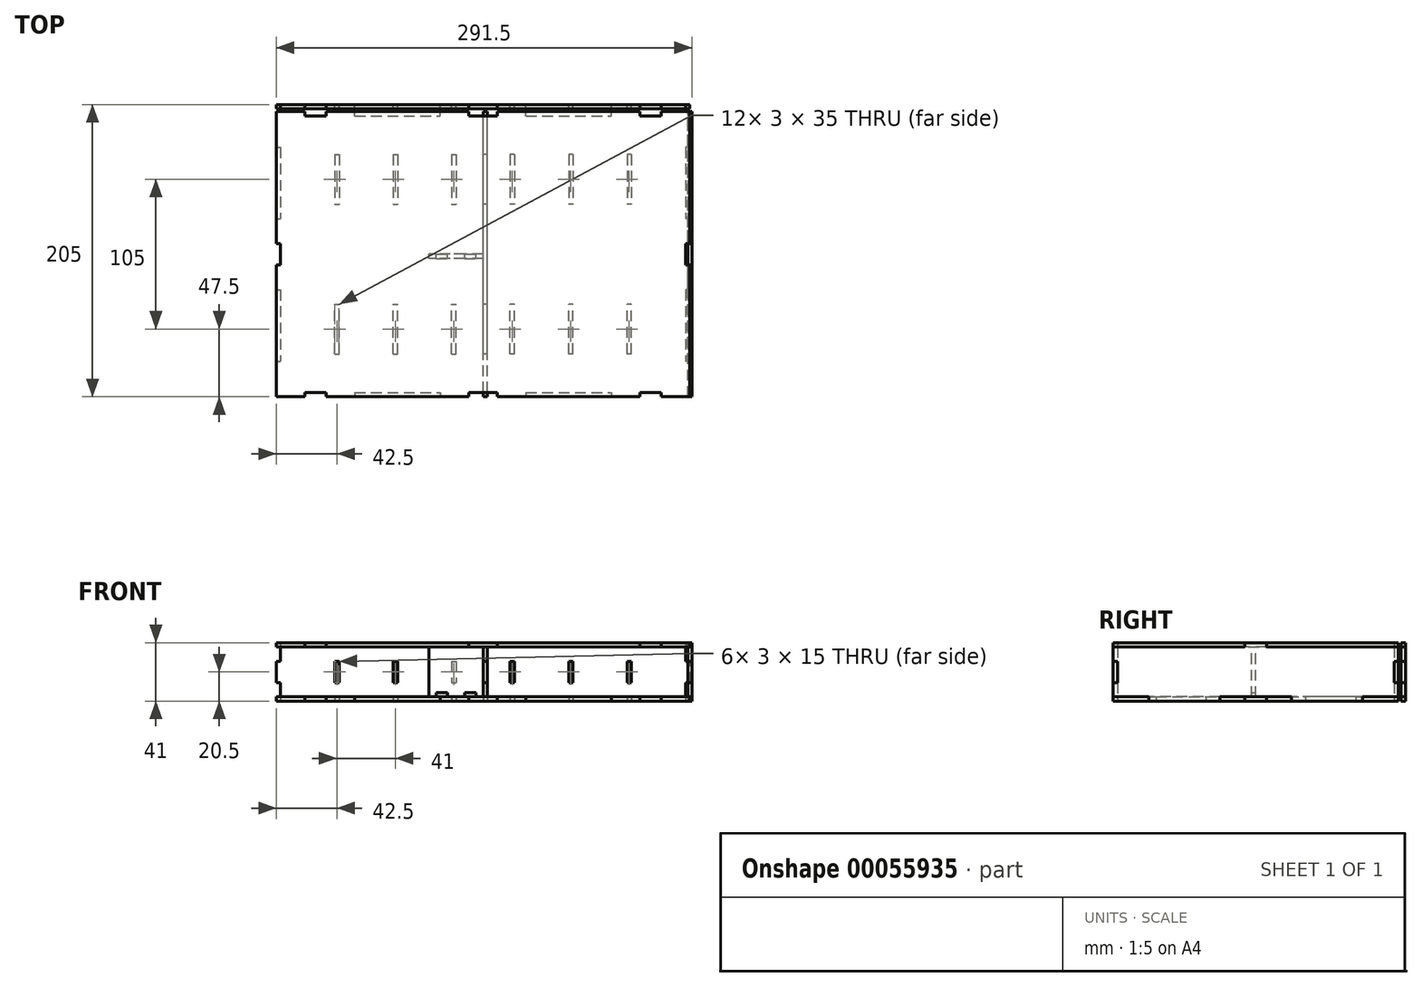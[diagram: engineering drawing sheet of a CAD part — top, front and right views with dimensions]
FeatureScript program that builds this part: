
annotation { "Feature Type Name" : "Feature", "Feature Type Description" : "" }
export const myFeature = defineFeature(function(context is Context, id is Id, definition is map)
    precondition{}
    {
        {
            assignVariable(context, id + "F0", {"name" : "WoodWidth", "anyValue" : 3});
        }
        {
            var Q0;
            Q0=qCreatedBy(makeId("Top.planeOp"),FACE);
            var sketch = newSketch(context, id + "F1", { "sketchPlane" : qUnion([Q0])});
            skLineSegment(sketch, "E0.bottom", {"start": v(-145, 100) * mm, "end": v(-125, 100) * mm});
            skLineSegment(sketch, "E0.top", {"start": v(-145, -100) * mm, "end": v(-125, -100) * mm});
            skLineSegment(sketch, "E0.left", {"start": v(-145, 100) * mm, "end": v(-145, 75) * mm});
            skLineSegment(sketch, "E0.right", {"start": v(145, 100) * mm, "end": v(145, 75) * mm});
            skLineSegment(sketch, "E1.bottom", {"start": v(-125, 97) * mm, "end": v(-110, 97) * mm});
            skLineSegment(sketch, "E1.top", {"start": v(-125, -97) * mm, "end": v(-110, -97) * mm});
            skLineSegment(sketch, "E1.left", {"start": v(-142, 75) * mm, "end": v(-142, 25) * mm});
            skLineSegment(sketch, "E1.right", {"start": v(142, 75) * mm, "end": v(142, 25) * mm});
            skLineSegment(sketch, "E2.bottom", {"start": v(-145, 75) * mm, "end": v(-142, 75) * mm});
            skLineSegment(sketch, "E2.top", {"start": v(-145, 25) * mm, "end": v(-142, 25) * mm});
            skLineSegment(sketch, "E3.MirrorCS", {"start": v(-145, -25) * mm, "end": v(-142, -25) * mm});
            skLineSegment(sketch, "E4.MirrorCS", {"start": v(-145, -75) * mm, "end": v(-142, -75) * mm});
            skLineSegment(sketch, "E5.MirrorCS", {"start": v(145, 75) * mm, "end": v(142, 75) * mm});
            skLineSegment(sketch, "E6.MirrorCS", {"start": v(145, 25) * mm, "end": v(142, 25) * mm});
            skLineSegment(sketch, "E7.MirrorCS", {"start": v(145, -25) * mm, "end": v(142, -25) * mm});
            skLineSegment(sketch, "E8.MirrorCS", {"start": v(145, -75) * mm, "end": v(142, -75) * mm});
            skLineSegment(sketch, "E9", {"start": v(-30, 97) * mm, "end": v(-30, 100) * mm});
            skLineSegment(sketch, "E10", {"start": v(-90, 97) * mm, "end": v(-90, 100) * mm});
            skLineSegment(sketch, "E11.MirrorCS", {"start": v(30, 97) * mm, "end": v(30, 100) * mm});
            skLineSegment(sketch, "E12.MirrorCS", {"start": v(90, 97) * mm, "end": v(90, 100) * mm});
            skLineSegment(sketch, "E13.MirrorCS", {"start": v(-30, -97) * mm, "end": v(-30, -100) * mm});
            skLineSegment(sketch, "E14.MirrorCS", {"start": v(-90, -97) * mm, "end": v(-90, -100) * mm});
            skLineSegment(sketch, "E15.MirrorCS", {"start": v(30, -97) * mm, "end": v(30, -100) * mm});
            skLineSegment(sketch, "E16.MirrorCS", {"start": v(90, -97) * mm, "end": v(90, -100) * mm});
            skLineSegment(sketch, "E17.trimOffspring", {"start": v(-30, 100) * mm, "end": v(-10, 100) * mm});
            skLineSegment(sketch, "E18.trimOffspring", {"start": v(90, 100) * mm, "end": v(110, 100) * mm});
            skLineSegment(sketch, "E19.trimOffspring", {"start": v(-145, 25) * mm, "end": v(-145, 7.5) * mm});
            skLineSegment(sketch, "E20.trimOffspring", {"start": v(-145, -75) * mm, "end": v(-145, -100) * mm});
            skLineSegment(sketch, "E21.trimOffspring", {"start": v(-30, -100) * mm, "end": v(-10, -100) * mm});
            skLineSegment(sketch, "E22.trimOffspring", {"start": v(90, -100) * mm, "end": v(110, -100) * mm});
            skLineSegment(sketch, "E23.trimOffspring", {"start": v(145, -75) * mm, "end": v(145, -100) * mm});
            skLineSegment(sketch, "E24.trimOffspring", {"start": v(145, 25) * mm, "end": v(145, 7.5) * mm});
            skLineSegment(sketch, "E25", {"start": v(-10, 100) * mm, "end": v(-10, 97) * mm});
            skLineSegment(sketch, "E26", {"start": v(-145, 7.5) * mm, "end": v(-142, 7.5) * mm});
            skLineSegment(sketch, "E27", {"start": v(-125, 100) * mm, "end": v(-125, 97) * mm});
            skLineSegment(sketch, "E28", {"start": v(-110, 100) * mm, "end": v(-110, 97) * mm});
            skLineSegment(sketch, "E29.MirrorCS", {"start": v(145, 7.5) * mm, "end": v(142, 7.5) * mm});
            skLineSegment(sketch, "E30.MirrorCS", {"start": v(10, 100) * mm, "end": v(10, 97) * mm});
            skLineSegment(sketch, "E31.MirrorCS", {"start": v(110, 100) * mm, "end": v(110, 97) * mm});
            skLineSegment(sketch, "E32.MirrorCS", {"start": v(125, 100) * mm, "end": v(125, 97) * mm});
            skLineSegment(sketch, "E33.MirrorCS", {"start": v(-145, -7.5) * mm, "end": v(-142, -7.5) * mm});
            skLineSegment(sketch, "E34.MirrorCS", {"start": v(-125, -100) * mm, "end": v(-125, -97) * mm});
            skLineSegment(sketch, "E35.MirrorCS", {"start": v(-110, -100) * mm, "end": v(-110, -97) * mm});
            skLineSegment(sketch, "E36.MirrorCS", {"start": v(-10, -100) * mm, "end": v(-10, -97) * mm});
            skLineSegment(sketch, "E37.MirrorCS", {"start": v(10, -100) * mm, "end": v(10, -97) * mm});
            skLineSegment(sketch, "E38.MirrorCS", {"start": v(110, -100) * mm, "end": v(110, -97) * mm});
            skLineSegment(sketch, "E39.MirrorCS", {"start": v(125, -100) * mm, "end": v(125, -97) * mm});
            skLineSegment(sketch, "E40.MirrorCS", {"start": v(145, -7.5) * mm, "end": v(142, -7.5) * mm});
            skLineSegment(sketch, "E41.trimOffspring", {"start": v(-110, 100) * mm, "end": v(-90, 100) * mm});
            skLineSegment(sketch, "E42.trimOffspring", {"start": v(10, 100) * mm, "end": v(30, 100) * mm});
            skLineSegment(sketch, "E43.trimOffspring", {"start": v(125, 100) * mm, "end": v(145, 100) * mm});
            skLineSegment(sketch, "E44.trimOffspring", {"start": v(145, -7.5) * mm, "end": v(145, -25) * mm});
            skLineSegment(sketch, "E45.trimOffspring", {"start": v(125, -100) * mm, "end": v(145, -100) * mm});
            skLineSegment(sketch, "E46.trimOffspring", {"start": v(10, -100) * mm, "end": v(30, -100) * mm});
            skLineSegment(sketch, "E47.trimOffspring", {"start": v(-110, -100) * mm, "end": v(-90, -100) * mm});
            skLineSegment(sketch, "E48.trimOffspring", {"start": v(-145, -7.5) * mm, "end": v(-145, -25) * mm});
            skPoint(sketch, "E49.orphan", {"position": v(-142, 97) * mm});
            skLineSegment(sketch, "E50.trimOffspring", {"start": v(-90, 97) * mm, "end": v(-30, 97) * mm});
            skLineSegment(sketch, "E51.trimOffspring", {"start": v(-10, 97) * mm, "end": v(10, 97) * mm});
            skLineSegment(sketch, "E52.trimOffspring", {"start": v(30, 97) * mm, "end": v(90, 97) * mm});
            skLineSegment(sketch, "E53.trimOffspring", {"start": v(110, 97) * mm, "end": v(125, 97) * mm});
            skLineSegment(sketch, "E54.trimOffspring", {"start": v(142, 7.5) * mm, "end": v(142, -7.5) * mm});
            skLineSegment(sketch, "E55.trimOffspring", {"start": v(142, -25) * mm, "end": v(142, -75) * mm});
            skLineSegment(sketch, "E56.trimOffspring", {"start": v(110, -97) * mm, "end": v(125, -97) * mm});
            skLineSegment(sketch, "E57.trimOffspring", {"start": v(30, -97) * mm, "end": v(90, -97) * mm});
            skLineSegment(sketch, "E58.trimOffspring", {"start": v(-10, -97) * mm, "end": v(10, -97) * mm});
            skLineSegment(sketch, "E59.trimOffspring", {"start": v(-90, -97) * mm, "end": v(-30, -97) * mm});
            skLineSegment(sketch, "E60.trimOffspring", {"start": v(-142, -25) * mm, "end": v(-142, -75) * mm});
            skLineSegment(sketch, "E61.trimOffspring", {"start": v(-142, 7.5) * mm, "end": v(-142, -7.5) * mm});
            skLineSegment(sketch, "E62.bottom", {"start": v(-104, 70) * mm, "end": v(-101, 70) * mm});
            skLineSegment(sketch, "E62.top", {"start": v(-104, 35) * mm, "end": v(-101, 35) * mm});
            skLineSegment(sketch, "E62.left", {"start": v(-104, 70) * mm, "end": v(-104, 35) * mm});
            skLineSegment(sketch, "E62.right", {"start": v(-101, 70) * mm, "end": v(-101, 35) * mm});
            skLineSegment(sketch, "E63.MirrorCS", {"start": v(-104, -35) * mm, "end": v(-101, -35) * mm});
            skLineSegment(sketch, "E64.MirrorCS", {"start": v(-101, -70) * mm, "end": v(-101, -35) * mm});
            skLineSegment(sketch, "E65.MirrorCS", {"start": v(-104, -70) * mm, "end": v(-104, -35) * mm});
            skLineSegment(sketch, "E66.MirrorCS", {"start": v(-104, -70) * mm, "end": v(-101, -70) * mm});
            skLineSegment(sketch, "E67.MirrorCS", {"start": v(104, 35) * mm, "end": v(101, 35) * mm});
            skLineSegment(sketch, "E68.MirrorCS", {"start": v(104, 70) * mm, "end": v(101, 70) * mm});
            skLineSegment(sketch, "E69.MirrorCS", {"start": v(101, 70) * mm, "end": v(101, 35) * mm});
            skLineSegment(sketch, "E70.MirrorCS", {"start": v(104, 70) * mm, "end": v(104, 35) * mm});
            skLineSegment(sketch, "E71.MirrorCS", {"start": v(104, -35) * mm, "end": v(101, -35) * mm});
            skLineSegment(sketch, "E72.MirrorCS", {"start": v(104, -70) * mm, "end": v(101, -70) * mm});
            skLineSegment(sketch, "E73.MirrorCS", {"start": v(101, -70) * mm, "end": v(101, -35) * mm});
            skLineSegment(sketch, "E74.MirrorCS", {"start": v(104, -70) * mm, "end": v(104, -35) * mm});
            skLineSegment(sketch, "E75.right", {"start": v(-63, 70) * mm, "end": v(-63, 35) * mm});
            skLineSegment(sketch, "E75.left", {"start": v(-60, 70) * mm, "end": v(-60, 35) * mm});
            skLineSegment(sketch, "E75.top", {"start": v(-63, 35) * mm, "end": v(-60, 35) * mm});
            skLineSegment(sketch, "E75.bottom", {"start": v(-63, 70) * mm, "end": v(-60, 70) * mm});
            skLineSegment(sketch, "E76.MirrorCS", {"start": v(63, 70) * mm, "end": v(60, 70) * mm});
            skLineSegment(sketch, "E77.MirrorCS", {"start": v(63, 35) * mm, "end": v(60, 35) * mm});
            skLineSegment(sketch, "E78.MirrorCS", {"start": v(60, 70) * mm, "end": v(60, 35) * mm});
            skLineSegment(sketch, "E79.MirrorCS", {"start": v(63, 70) * mm, "end": v(63, 35) * mm});
            skLineSegment(sketch, "E80.MirrorCS", {"start": v(63, -35) * mm, "end": v(60, -35) * mm});
            skLineSegment(sketch, "E81.MirrorCS", {"start": v(-63, -70) * mm, "end": v(-60, -70) * mm});
            skLineSegment(sketch, "E82.MirrorCS", {"start": v(63, -70) * mm, "end": v(60, -70) * mm});
            skLineSegment(sketch, "E83.MirrorCS", {"start": v(-63, -35) * mm, "end": v(-60, -35) * mm});
            skLineSegment(sketch, "E84.MirrorCS", {"start": v(60, -70) * mm, "end": v(60, -35) * mm});
            skLineSegment(sketch, "E85.MirrorCS", {"start": v(-63, -70) * mm, "end": v(-63, -35) * mm});
            skLineSegment(sketch, "E86.MirrorCS", {"start": v(63, -70) * mm, "end": v(63, -35) * mm});
            skLineSegment(sketch, "E87.MirrorCS", {"start": v(-60, -70) * mm, "end": v(-60, -35) * mm});
            skLineSegment(sketch, "E88.right", {"start": v(-22, 70) * mm, "end": v(-22, 35) * mm});
            skLineSegment(sketch, "E88.left", {"start": v(-19, 70) * mm, "end": v(-19, 35) * mm});
            skLineSegment(sketch, "E88.bottom", {"start": v(-22, 70) * mm, "end": v(-19, 70) * mm});
            skLineSegment(sketch, "E88.top", {"start": v(-22, 35) * mm, "end": v(-19, 35) * mm});
            skLineSegment(sketch, "E89.MirrorCS", {"start": v(22, 35) * mm, "end": v(19, 35) * mm});
            skLineSegment(sketch, "E90.MirrorCS", {"start": v(22, 70) * mm, "end": v(19, 70) * mm});
            skLineSegment(sketch, "E91.MirrorCS", {"start": v(19, 70) * mm, "end": v(19, 35) * mm});
            skLineSegment(sketch, "E92.MirrorCS", {"start": v(22, 70) * mm, "end": v(22, 35) * mm});
            skLineSegment(sketch, "E93.MirrorCS", {"start": v(-22, -35) * mm, "end": v(-19, -35) * mm});
            skLineSegment(sketch, "E94.MirrorCS", {"start": v(22, -35) * mm, "end": v(19, -35) * mm});
            skLineSegment(sketch, "E95.MirrorCS", {"start": v(22, -70) * mm, "end": v(19, -70) * mm});
            skLineSegment(sketch, "E96.MirrorCS", {"start": v(-22, -70) * mm, "end": v(-19, -70) * mm});
            skLineSegment(sketch, "E97.MirrorCS", {"start": v(22, -70) * mm, "end": v(22, -35) * mm});
            skLineSegment(sketch, "E98.MirrorCS", {"start": v(-22, -70) * mm, "end": v(-22, -35) * mm});
            skLineSegment(sketch, "E99.MirrorCS", {"start": v(-19, -70) * mm, "end": v(-19, -35) * mm});
            skLineSegment(sketch, "E100.MirrorCS", {"start": v(19, -70) * mm, "end": v(19, -35) * mm});
            skSolve(sketch);
        }
        {
            var Q0;
            {var subQ13=sQuery(id+"F1.wireOp",EDGE,"E1.left");Q0=makeQuery(id+"F1.imprint","IMPRINT",FACE,{"disambiguationData":[TD([[makeQuery(id+"F1.imprint","IMPRINT",EDGE,{"derivedFrom":subQ13}),1.0]])]});}
            var Q1;
            Q1=makeQuery(id+"F1.imprint","IMPRINT",FACE,{"disambiguationData":[TD([[makeQuery(id+"F1.imprint","IMPRINT",EDGE,{"derivedFrom":sQuery(id+"F1.wireOp",EDGE,"E0.bottom")}),-1.0]])]});
            var Q2;
            {var subQ0=sQuery(id+"F1.wireOp",EDGE,"E9");Q2=makeQuery(id+"F1.imprint","IMPRINT",FACE,{"disambiguationData":[TD([[makeQuery(id+"F1.imprint","IMPRINT",EDGE,{"derivedFrom":subQ0}),-1.0]])]});}
            var Q3;
            Q3=makeQuery(id+"F1.imprint","IMPRINT",FACE,{"disambiguationData":[TD([[makeQuery(id+"F1.imprint","IMPRINT",EDGE,{"derivedFrom":sQuery(id+"F1.wireOp",EDGE,"E0.right")}),-1.0]])]});
            var Q4;
            {var subQ0=sQuery(id+"F1.wireOp",EDGE,"E6.MirrorCS");Q4=makeQuery(id+"F1.imprint","IMPRINT",FACE,{"disambiguationData":[TD([[makeQuery(id+"F1.imprint","IMPRINT",EDGE,{"derivedFrom":subQ0}),1.0]])]});}
            var Q5;
            {var subQ1=sQuery(id+"F1.wireOp",EDGE,"E8.MirrorCS");Q5=makeQuery(id+"F1.imprint","IMPRINT",FACE,{"disambiguationData":[TD([[makeQuery(id+"F1.imprint","IMPRINT",EDGE,{"derivedFrom":subQ1}),1.0]])]});}
            var Q6;
            {var subQ0=sQuery(id+"F1.wireOp",EDGE,"E13.MirrorCS");Q6=makeQuery(id+"F1.imprint","IMPRINT",FACE,{"disambiguationData":[TD([[makeQuery(id+"F1.imprint","IMPRINT",EDGE,{"derivedFrom":subQ0}),1.0]])]});}
            var Q7;
            Q7=makeQuery(id+"F1.imprint","IMPRINT",FACE,{"disambiguationData":[TD([[makeQuery(id+"F1.imprint","IMPRINT",EDGE,{"derivedFrom":sQuery(id+"F1.wireOp",EDGE,"E0.top")}),1.0]])]});
            var Q8;
            {var subQ0=sQuery(id+"F1.wireOp",EDGE,"E2.top");Q8=makeQuery(id+"F1.imprint","IMPRINT",FACE,{"disambiguationData":[TD([[makeQuery(id+"F1.imprint","IMPRINT",EDGE,{"derivedFrom":subQ0}),-1.0]])]});}
            extrude(context, id + "F2", {"entities" : qUnion([Q0, Q1, Q2, Q3, Q4, Q5, Q6, Q7, Q8]), "depth" : (getVariable(context, 'WoodWidth')) * mm});
        }
        {
            var Q0;
            Q0=qCreatedBy(makeId("Right.planeOp"),FACE);
            var sketch = newSketch(context, id + "F3", { "sketchPlane" : qUnion([Q0])});
            skLineSegment(sketch, "E101.top", {"start": v(-100, 38) * mm, "end": v(-7.5, 38) * mm});
            skLineSegment(sketch, "E101.left", {"start": v(-100, 3) * mm, "end": v(-100, 13) * mm});
            skLineSegment(sketch, "E101.right", {"start": v(100, 3) * mm, "end": v(100, 13) * mm});
            skLineSegment(sketch, "E102", {"start": v(-75, 3) * mm, "end": v(-75, 0) * mm});
            skLineSegment(sketch, "E103", {"start": v(-25, 3) * mm, "end": v(-25, 0) * mm});
            skLineSegment(sketch, "E104.MirrorCS", {"start": v(25, 3) * mm, "end": v(25, 0) * mm});
            skLineSegment(sketch, "E105.MirrorCS", {"start": v(75, 3) * mm, "end": v(75, 0) * mm});
            skLineSegment(sketch, "E106", {"start": v(-97, 28) * mm, "end": v(-97, 13) * mm});
            skLineSegment(sketch, "E107", {"start": v(-100, 28) * mm, "end": v(-97, 28) * mm});
            skLineSegment(sketch, "E108", {"start": v(-100, 13) * mm, "end": v(-97, 13) * mm});
            skLineSegment(sketch, "E109.MirrorCS", {"start": v(100, 13) * mm, "end": v(97, 13) * mm});
            skLineSegment(sketch, "E110.MirrorCS", {"start": v(100, 28) * mm, "end": v(97, 28) * mm});
            skLineSegment(sketch, "E111.MirrorCS", {"start": v(97, 28) * mm, "end": v(97, 13) * mm});
            skLineSegment(sketch, "E112.trimOffspring", {"start": v(-100, 28) * mm, "end": v(-100, 38) * mm});
            skPoint(sketch, "E113.orphan", {"position": v(-100, 3) * mm});
            skPoint(sketch, "E114.orphan", {"position": v(-97, 0) * mm});
            skLineSegment(sketch, "E115.trimOffspring", {"start": v(100, 28) * mm, "end": v(100, 38) * mm});
            skPoint(sketch, "E116.orphan", {"position": v(97, 38) * mm});
            skPoint(sketch, "E117.trimOffspring.end.orphan", {"position": v(97, 0) * mm});
            skPoint(sketch, "E118.orphan", {"position": v(-97, 38) * mm});
            skLineSegment(sketch, "E119", {"start": v(-100, 3) * mm, "end": v(-75, 3) * mm});
            skLineSegment(sketch, "E120", {"start": v(75, 0) * mm, "end": v(25, 0) * mm});
            skPoint(sketch, "E121.orphan", {"position": v(-100, 0) * mm});
            skLineSegment(sketch, "E122.trimOffspring", {"start": v(-25, 0) * mm, "end": v(-75, 0) * mm});
            skLineSegment(sketch, "E123.trimOffspring", {"start": v(75, 3) * mm, "end": v(100, 3) * mm});
            skLineSegment(sketch, "E124", {"start": v(-7.5, 38) * mm, "end": v(-7.5, 41) * mm});
            skLineSegment(sketch, "E125", {"start": v(-7.5, 41) * mm, "end": v(0, 41) * mm});
            skLineSegment(sketch, "E126.MirrorCS", {"start": v(7.5, 41) * mm, "end": v(0, 41) * mm});
            skLineSegment(sketch, "E127.MirrorCS", {"start": v(7.5, 38) * mm, "end": v(7.5, 41) * mm});
            skLineSegment(sketch, "E128.trimOffspring", {"start": v(7.5, 38) * mm, "end": v(100, 38) * mm});
            skLineSegment(sketch, "E129", {"start": v(-25, 3) * mm, "end": v(25, 3) * mm});
            skSolve(sketch);
        }
        {
            var Q0;
            Q0=makeQuery(id+"F3.imprint","IMPRINT",FACE,{"disambiguationData":[TD([[makeQuery(id+"F3.imprint","IMPRINT",EDGE,{"derivedFrom":sQuery(id+"F3.wireOp",EDGE,"E101.top")}),-1.0]])]});
            extrude(context, id + "F4", {"entities" : qUnion([Q0]), "depth" : (getVariable(context, 'WoodWidth')) * mm});
        }
        {
            var Q0;
            Q0=makeQuery(id+"F4.opExtrude","SWEPT_BODY",BODY,{"disambiguationData":[OSD([sQuery(id+"F3.wireOp",EDGE,"E101.top"),sQuery(id+"F3.wireOp",EDGE,"E101.left"),sQuery(id+"F3.wireOp",EDGE,"E101.right"),sQuery(id+"F3.wireOp",EDGE,"E102"),sQuery(id+"F3.wireOp",EDGE,"E103"),sQuery(id+"F3.wireOp",EDGE,"cdd6de69-b75f-463d-88d1-304e89352a25"),sQuery(id+"F3.wireOp",EDGE,"cb626959-0f36-4611-9174-e5582c259fc60.MirrorCS"),sQuery(id+"F3.wireOp",EDGE,"E104.MirrorCS"),sQuery(id+"F3.wireOp",EDGE,"E105.MirrorCS"),sQuery(id+"F3.wireOp",EDGE,"E106"),sQuery(id+"F3.wireOp",EDGE,"E107"),sQuery(id+"F3.wireOp",EDGE,"E108"),sQuery(id+"F3.wireOp",EDGE,"E109.MirrorCS"),sQuery(id+"F3.wireOp",EDGE,"E110.MirrorCS"),sQuery(id+"F3.wireOp",EDGE,"E111.MirrorCS"),sQuery(id+"F3.wireOp",EDGE,"E112.trimOffspring"),sQuery(id+"F3.wireOp",EDGE,"E115.trimOffspring"),sQuery(id+"F3.wireOp",EDGE,"E119"),sQuery(id+"F3.wireOp",EDGE,"E120"),sQuery(id+"F3.wireOp",EDGE,"E122.trimOffspring"),sQuery(id+"F3.wireOp",EDGE,"c6658c1a-ea69-4595-8e1a-c0dab725dcbe.trimOffspring"),sQuery(id+"F3.wireOp",EDGE,"E123.trimOffspring"),sQuery(id+"F3.wireOp",EDGE,"9fd187d6-3b35-4cf2-808b-338c497833ee.trimOffspring"),sQuery(id+"F3.wireOp",EDGE,"23121bdd-483d-45c2-8d1b-d883080a6cf4.trimOffspring"),sQuery(id+"F3.wireOp",EDGE,"E124"),sQuery(id+"F3.wireOp",EDGE,"E125"),sQuery(id+"F3.wireOp",EDGE,"E126.MirrorCS"),sQuery(id+"F3.wireOp",EDGE,"E127.MirrorCS"),sQuery(id+"F3.wireOp",EDGE,"E128.trimOffspring")])]});
            transform(context, id + "F5", {"entities" : qUnion([Q0]), "transformType" : TransformType.TRANSLATION_3D, "dx" : (297 / 2 - 5) * mm, "dy" : 0 * mm, "dz" : 0 * mm, "makeCopy" : false});
        }
        {
            var Q0;
            Q0=qCreatedBy(makeId("Front.planeOp"),FACE);
            var sketch = newSketch(context, id + "F6", { "sketchPlane" : qUnion([Q0])});
            skLineSegment(sketch, "E130.top", {"start": v(-142, 38) * mm, "end": v(-125, 38) * mm});
            skLineSegment(sketch, "E130.left", {"start": v(-145, 13) * mm, "end": v(-145, 28) * mm});
            skLineSegment(sketch, "E131", {"start": v(142, 38) * mm, "end": v(142, 28) * mm});
            skLineSegment(sketch, "E132", {"start": v(-30, 3) * mm, "end": v(-30, 0) * mm});
            skLineSegment(sketch, "E133", {"start": v(-90, 3) * mm, "end": v(-90, 0) * mm});
            skLineSegment(sketch, "E134", {"start": v(142, 28) * mm, "end": v(145, 28) * mm});
            skLineSegment(sketch, "E135", {"start": v(145, 13) * mm, "end": v(142, 13) * mm});
            skLineSegment(sketch, "E136.MirrorCS", {"start": v(30, 3) * mm, "end": v(30, 0) * mm});
            skLineSegment(sketch, "E137.MirrorCS", {"start": v(90, 3) * mm, "end": v(90, 0) * mm});
            skLineSegment(sketch, "E138.MirrorCS", {"start": v(-142, 38) * mm, "end": v(-142, 28) * mm});
            skLineSegment(sketch, "E139.MirrorCS", {"start": v(-145, 13) * mm, "end": v(-142, 13) * mm});
            skLineSegment(sketch, "E140.MirrorCS", {"start": v(-142, 28) * mm, "end": v(-145, 28) * mm});
            skPoint(sketch, "E141.orphan", {"position": v(148.5, 38) * mm});
            skLineSegment(sketch, "E142.trimOffspring", {"start": v(145, 13) * mm, "end": v(145, 28) * mm});
            skPoint(sketch, "E130.right.end.orphan", {"position": v(148.5, 5) * mm});
            skLineSegment(sketch, "E143.trimOffspring", {"start": v(30, 0) * mm, "end": v(90, 0) * mm});
            skLineSegment(sketch, "E144.trimOffspring", {"start": v(-90, 0) * mm, "end": v(-30, 0) * mm});
            skPoint(sketch, "E145.orphan", {"position": v(-145, 38) * mm});
            skPoint(sketch, "E146.orphan", {"position": v(-145, 5) * mm});
            skLineSegment(sketch, "E147.trimOffspring", {"start": v(142, 13) * mm, "end": v(142, 3) * mm});
            skLineSegment(sketch, "E148.trimOffspring", {"start": v(-142, 13) * mm, "end": v(-142, 3) * mm});
            skLineSegment(sketch, "E149", {"start": v(-10, 38) * mm, "end": v(-10, 41) * mm});
            skLineSegment(sketch, "E150", {"start": v(-10, 41) * mm, "end": v(10, 41) * mm});
            skLineSegment(sketch, "E151", {"start": v(10, 41) * mm, "end": v(10, 38) * mm});
            skLineSegment(sketch, "E152", {"start": v(-110, 41) * mm, "end": v(-110, 38) * mm});
            skLineSegment(sketch, "E153.MirrorCS", {"start": v(110, 41) * mm, "end": v(110, 38) * mm});
            skLineSegment(sketch, "E154.trimOffspring", {"start": v(-90, 38) * mm, "end": v(-10, 38) * mm});
            skLineSegment(sketch, "E155.trimOffspring", {"start": v(10, 38) * mm, "end": v(90, 38) * mm});
            skLineSegment(sketch, "E156.trimOffspring", {"start": v(125, 38) * mm, "end": v(142, 38) * mm});
            skLineSegment(sketch, "E157", {"start": v(-125, 38) * mm, "end": v(-125, 41) * mm});
            skLineSegment(sketch, "E158", {"start": v(-125, 41) * mm, "end": v(-110, 41) * mm});
            skLineSegment(sketch, "E159.MirrorCS", {"start": v(125, 41) * mm, "end": v(110, 41) * mm});
            skLineSegment(sketch, "E160.MirrorCS", {"start": v(125, 38) * mm, "end": v(125, 41) * mm});
            skLineSegment(sketch, "E161", {"start": v(-110, 38) * mm, "end": v(-90, 38) * mm});
            skLineSegment(sketch, "E162", {"start": v(90, 38) * mm, "end": v(110, 38) * mm});
            skPoint(sketch, "E163.MirrorCS.end.orphan", {"position": v(110, 41) * mm});
            skLineSegment(sketch, "E164", {"start": v(142, 3) * mm, "end": v(90, 3) * mm});
            skLineSegment(sketch, "E165", {"start": v(30, 3) * mm, "end": v(-30, 3) * mm});
            skLineSegment(sketch, "E166", {"start": v(-90, 3) * mm, "end": v(-142, 3) * mm});
            skLineSegment(sketch, "E167.bottom", {"start": v(-104, 28) * mm, "end": v(-101, 28) * mm});
            skLineSegment(sketch, "E167.top", {"start": v(-104, 13) * mm, "end": v(-101, 13) * mm});
            skLineSegment(sketch, "E167.left", {"start": v(-104, 28) * mm, "end": v(-104, 13) * mm});
            skLineSegment(sketch, "E167.right", {"start": v(-101, 28) * mm, "end": v(-101, 13) * mm});
            skLineSegment(sketch, "E168.bottom", {"start": v(-63, 28) * mm, "end": v(-60, 28) * mm});
            skLineSegment(sketch, "E168.top", {"start": v(-63, 13) * mm, "end": v(-60, 13) * mm});
            skLineSegment(sketch, "E168.right", {"start": v(-60, 28) * mm, "end": v(-60, 13) * mm});
            skLineSegment(sketch, "E168.left", {"start": v(-63, 28) * mm, "end": v(-63, 13) * mm});
            skLineSegment(sketch, "E169.bottom", {"start": v(-22, 28) * mm, "end": v(-19, 28) * mm});
            skLineSegment(sketch, "E169.top", {"start": v(-22, 13) * mm, "end": v(-19, 13) * mm});
            skLineSegment(sketch, "E169.right", {"start": v(-19, 28) * mm, "end": v(-19, 13) * mm});
            skLineSegment(sketch, "E169.left", {"start": v(-22, 28) * mm, "end": v(-22, 13) * mm});
            skLineSegment(sketch, "E170.MirrorCS", {"start": v(22, 13) * mm, "end": v(19, 13) * mm});
            skLineSegment(sketch, "E171.MirrorCS", {"start": v(104, 28) * mm, "end": v(101, 28) * mm});
            skLineSegment(sketch, "E172.MirrorCS", {"start": v(104, 13) * mm, "end": v(101, 13) * mm});
            skLineSegment(sketch, "E173.MirrorCS", {"start": v(22, 28) * mm, "end": v(19, 28) * mm});
            skLineSegment(sketch, "E174.MirrorCS", {"start": v(63, 28) * mm, "end": v(60, 28) * mm});
            skLineSegment(sketch, "E175.MirrorCS", {"start": v(63, 13) * mm, "end": v(60, 13) * mm});
            skLineSegment(sketch, "E176.MirrorCS", {"start": v(63, 28) * mm, "end": v(63, 13) * mm});
            skLineSegment(sketch, "E177.MirrorCS", {"start": v(60, 28) * mm, "end": v(60, 13) * mm});
            skLineSegment(sketch, "E178.MirrorCS", {"start": v(104, 28) * mm, "end": v(104, 13) * mm});
            skLineSegment(sketch, "E179.MirrorCS", {"start": v(22, 28) * mm, "end": v(22, 13) * mm});
            skLineSegment(sketch, "E180.MirrorCS", {"start": v(101, 28) * mm, "end": v(101, 13) * mm});
            skLineSegment(sketch, "E181.MirrorCS", {"start": v(19, 28) * mm, "end": v(19, 13) * mm});
            skSolve(sketch);
        }
        {
            var Q0;
            Q0=makeQuery(id+"F6.imprint","IMPRINT",FACE,{"disambiguationData":[TD([[makeQuery(id+"F6.imprint","IMPRINT",EDGE,{"derivedFrom":sQuery(id+"F6.wireOp",EDGE,"E130.top")}),-1.0]])]});
            extrude(context, id + "F7", {"entities" : qUnion([Q0]), "depth" : (getVariable(context, 'WoodWidth')) * mm});
        }
        {
            var Q0;
            Q0=makeQuery(id+"F7.opExtrude","SWEPT_BODY",BODY,{"disambiguationData":[OSD([sQuery(id+"F6.wireOp",EDGE,"E130.bottom"),sQuery(id+"F6.wireOp",EDGE,"E130.top"),sQuery(id+"F6.wireOp",EDGE,"E130.left"),sQuery(id+"F6.wireOp",EDGE,"863d3b8a-d14c-4461-88c4-5134910bc86d"),sQuery(id+"F6.wireOp",EDGE,"E131"),sQuery(id+"F6.wireOp",EDGE,"5721f5ff-d7d6-4be2-a35f-81ddbb97a744"),sQuery(id+"F6.wireOp",EDGE,"E132"),sQuery(id+"F6.wireOp",EDGE,"E133"),sQuery(id+"F6.wireOp",EDGE,"5b2e436f-17fc-4a67-aee5-f1bbab5932e6"),sQuery(id+"F6.wireOp",EDGE,"3058391f-3380-4d63-85c0-ff2ec9b04228"),sQuery(id+"F6.wireOp",EDGE,"E134"),sQuery(id+"F6.wireOp",EDGE,"E135"),sQuery(id+"F6.wireOp",EDGE,"06b62deb-3f7e-462c-87f0-bffc6018c9340.MirrorCS"),sQuery(id+"F6.wireOp",EDGE,"E136.MirrorCS"),sQuery(id+"F6.wireOp",EDGE,"E137.MirrorCS"),sQuery(id+"F6.wireOp",EDGE,"7eebd4b8-8446-4496-bcb5-e3dce19aec800.MirrorCS"),sQuery(id+"F6.wireOp",EDGE,"c76f16e5-df2c-41a4-a324-e09e6eed5f7e0.MirrorCS"),sQuery(id+"F6.wireOp",EDGE,"E138.MirrorCS"),sQuery(id+"F6.wireOp",EDGE,"E139.MirrorCS"),sQuery(id+"F6.wireOp",EDGE,"E140.MirrorCS"),sQuery(id+"F6.wireOp",EDGE,"E142.trimOffspring"),sQuery(id+"F6.wireOp",EDGE,"1433ab13-8b9f-4c4e-8bdb-3c748ba6e6fb.trimOffspring"),sQuery(id+"F6.wireOp",EDGE,"E143.trimOffspring"),sQuery(id+"F6.wireOp",EDGE,"71df51e1-e505-4dfe-a91e-4d9923cb236f.trimOffspring"),sQuery(id+"F6.wireOp",EDGE,"E144.trimOffspring"),sQuery(id+"F6.wireOp",EDGE,"f454dcae-51a4-4539-ba63-113f1040b0c6.trimOffspring"),sQuery(id+"F6.wireOp",EDGE,"1a16d243-1e98-436a-8971-c0ea7fb50ce3.trimOffspring"),sQuery(id+"F6.wireOp",EDGE,"f5fd9031-82d8-4a74-9a41-0dfd1c9f76f4.trimOffspring"),sQuery(id+"F6.wireOp",EDGE,"150b176e-f1b8-4ab8-8c6b-ab155f0a05c3.trimOffspring"),sQuery(id+"F6.wireOp",EDGE,"0e241c9f-8b31-408f-bf2b-fcaa24491f50.trimOffspring"),sQuery(id+"F6.wireOp",EDGE,"E147.trimOffspring"),sQuery(id+"F6.wireOp",EDGE,"E148.trimOffspring")])]});
            transform(context, id + "F8", {"entities" : qUnion([Q0]), "transformType" : TransformType.TRANSLATION_3D, "dx" : 0 * mm, "dy" : (210 / 2) * mm, "dz" : 0 * mm, "makeCopy" : false});
        }
        {
            var Q0;
            Q0=qCreatedBy(makeId("Right.planeOp"),FACE);
            var sketch = newSketch(context, id + "F9", { "sketchPlane" : qUnion([Q0])});
            skLineSegment(sketch, "E182.bottom", {"start": v(-97, 38) * mm, "end": v(97, 38) * mm});
            skLineSegment(sketch, "E182.top", {"start": v(-70, 0) * mm, "end": v(-35, 0) * mm});
            skLineSegment(sketch, "E182.left", {"start": v(-100, 28) * mm, "end": v(-100, 13) * mm});
            skLineSegment(sketch, "E182.right", {"start": v(100, 28) * mm, "end": v(100, 13) * mm});
            skLineSegment(sketch, "E183", {"start": v(-97, 38) * mm, "end": v(-97, 3) * mm});
            skLineSegment(sketch, "E184", {"start": v(97, 38) * mm, "end": v(97, 3) * mm});
            skLineSegment(sketch, "E185", {"start": v(-97, 3) * mm, "end": v(97, 3) * mm});
            skLineSegment(sketch, "E186", {"start": v(-100, 13) * mm, "end": v(-97, 13) * mm});
            skLineSegment(sketch, "E187", {"start": v(-100, 28) * mm, "end": v(-97, 28) * mm});
            skLineSegment(sketch, "E188", {"start": v(-70, 3) * mm, "end": v(-70, 0) * mm});
            skLineSegment(sketch, "E189", {"start": v(-35, 3) * mm, "end": v(-35, 0) * mm});
            skLineSegment(sketch, "E190.MirrorCS", {"start": v(35, 3) * mm, "end": v(35, 0) * mm});
            skLineSegment(sketch, "E191.MirrorCS", {"start": v(70, 3) * mm, "end": v(70, 0) * mm});
            skLineSegment(sketch, "E192.MirrorCS", {"start": v(100, 13) * mm, "end": v(97, 13) * mm});
            skLineSegment(sketch, "E193.MirrorCS", {"start": v(100, 28) * mm, "end": v(97, 28) * mm});
            skPoint(sketch, "E194.orphan", {"position": v(-100, 38) * mm});
            skLineSegment(sketch, "E195.trimOffspring", {"start": v(35, 0) * mm, "end": v(70, 0) * mm});
            skPoint(sketch, "E196.orphan", {"position": v(100, 38) * mm});
            skSolve(sketch);
        }
        {
            var Q0;
            Q0 = qSketchRegion(id + "F9", true);
            extrude(context, id + "F10", {"entities" : qUnion([Q0]), "depth" : (getVariable(context, 'WoodWidth')) * mm});
        }
        {
            var Q0;
            Q0=qCreatedBy(makeId("Top.planeOp"),FACE);
            var sketch = newSketch(context, id + "F11", { "sketchPlane" : qUnion([Q0])});
            skLineSegment(sketch, "E197.bottom", {"start": v(-145, 100) * mm, "end": v(-125, 100) * mm});
            skLineSegment(sketch, "E197.top", {"start": v(-145, -100) * mm, "end": v(-125, -100) * mm});
            skLineSegment(sketch, "E197.left", {"start": v(-145, 100) * mm, "end": v(-145, 7.5) * mm});
            skLineSegment(sketch, "E197.right", {"start": v(145, 100) * mm, "end": v(145, 7.5) * mm});
            skLineSegment(sketch, "E198", {"start": v(-125, 100) * mm, "end": v(-125, 97) * mm});
            skLineSegment(sketch, "E199", {"start": v(-125, 97) * mm, "end": v(-110, 97) * mm});
            skLineSegment(sketch, "E200", {"start": v(-110, 97) * mm, "end": v(-110, 100) * mm});
            skLineSegment(sketch, "E201", {"start": v(-10, 100) * mm, "end": v(-10, 97) * mm});
            skLineSegment(sketch, "E202", {"start": v(-10, 97) * mm, "end": v(10, 97) * mm});
            skLineSegment(sketch, "E203", {"start": v(10, 97) * mm, "end": v(10, 100) * mm});
            skLineSegment(sketch, "E204", {"start": v(-145, 7.5) * mm, "end": v(-142, 7.5) * mm});
            skLineSegment(sketch, "E205", {"start": v(-142, 7.5) * mm, "end": v(-142, -7.5) * mm});
            skLineSegment(sketch, "E206", {"start": v(-142, -7.5) * mm, "end": v(-145, -7.5) * mm});
            skLineSegment(sketch, "E207.MirrorCS", {"start": v(10, -97) * mm, "end": v(10, -100) * mm});
            skLineSegment(sketch, "E208.MirrorCS", {"start": v(-10, -100) * mm, "end": v(-10, -97) * mm});
            skLineSegment(sketch, "E209.MirrorCS", {"start": v(-110, -97) * mm, "end": v(-110, -100) * mm});
            skLineSegment(sketch, "E210.MirrorCS", {"start": v(-125, -100) * mm, "end": v(-125, -97) * mm});
            skLineSegment(sketch, "E211.MirrorCS", {"start": v(-10, -97) * mm, "end": v(10, -97) * mm});
            skLineSegment(sketch, "E212.MirrorCS", {"start": v(-125, -97) * mm, "end": v(-110, -97) * mm});
            skLineSegment(sketch, "E213.MirrorCS", {"start": v(142, -7.5) * mm, "end": v(145, -7.5) * mm});
            skLineSegment(sketch, "E214.MirrorCS", {"start": v(142, 7.5) * mm, "end": v(142, -7.5) * mm});
            skLineSegment(sketch, "E215.MirrorCS", {"start": v(145, 7.5) * mm, "end": v(142, 7.5) * mm});
            skLineSegment(sketch, "E216.MirrorCS", {"start": v(110, 97) * mm, "end": v(110, 100) * mm});
            skLineSegment(sketch, "E217.MirrorCS", {"start": v(125, 97) * mm, "end": v(110, 97) * mm});
            skLineSegment(sketch, "E218.MirrorCS", {"start": v(125, 100) * mm, "end": v(125, 97) * mm});
            skLineSegment(sketch, "E219.MirrorCS", {"start": v(110, -97) * mm, "end": v(110, -100) * mm});
            skLineSegment(sketch, "E220.MirrorCS", {"start": v(125, -97) * mm, "end": v(110, -97) * mm});
            skLineSegment(sketch, "E221.MirrorCS", {"start": v(125, -100) * mm, "end": v(125, -97) * mm});
            skLineSegment(sketch, "E222.trimOffspring", {"start": v(-110, 100) * mm, "end": v(-10, 100) * mm});
            skLineSegment(sketch, "E223.trimOffspring", {"start": v(10, 100) * mm, "end": v(110, 100) * mm});
            skLineSegment(sketch, "E224.trimOffspring", {"start": v(125, 100) * mm, "end": v(145, 100) * mm});
            skLineSegment(sketch, "E225.trimOffspring", {"start": v(145, -7.5) * mm, "end": v(145, -100) * mm});
            skLineSegment(sketch, "E226.trimOffspring", {"start": v(125, -100) * mm, "end": v(145, -100) * mm});
            skLineSegment(sketch, "E227.trimOffspring", {"start": v(10, -100) * mm, "end": v(110, -100) * mm});
            skLineSegment(sketch, "E228.trimOffspring", {"start": v(-110, -100) * mm, "end": v(-10, -100) * mm});
            skLineSegment(sketch, "E229.trimOffspring", {"start": v(-145, -7.5) * mm, "end": v(-145, -100) * mm});
            skSolve(sketch);
        }
        {
            var Q0;
            Q0=makeQuery(id+"F11.imprint","IMPRINT",FACE,{"disambiguationData":[TD([[makeQuery(id+"F11.imprint","IMPRINT",EDGE,{"derivedFrom":sQuery(id+"F11.wireOp",EDGE,"E197.bottom")}),-1.0]])]});
            extrude(context, id + "F12", {"entities" : qUnion([Q0]), "depth" : (getVariable(context, 'WoodWidth')) * mm});
        }
        {
            var Q0;
            Q0=makeQuery(id+"F12.opExtrude","SWEPT_BODY",BODY,{"disambiguationData":[OSD([sQuery(id+"F11.wireOp",EDGE,"E197.bottom"),sQuery(id+"F11.wireOp",EDGE,"E197.left"),sQuery(id+"F11.wireOp",EDGE,"E197.right"),sQuery(id+"F11.wireOp",EDGE,"E198"),sQuery(id+"F11.wireOp",EDGE,"E199"),sQuery(id+"F11.wireOp",EDGE,"E200"),sQuery(id+"F11.wireOp",EDGE,"E201"),sQuery(id+"F11.wireOp",EDGE,"E202"),sQuery(id+"F11.wireOp",EDGE,"E203"),sQuery(id+"F11.wireOp",EDGE,"E204"),sQuery(id+"F11.wireOp",EDGE,"E205"),sQuery(id+"F11.wireOp",EDGE,"E206"),sQuery(id+"F11.wireOp",EDGE,"E207.MirrorCS"),sQuery(id+"F11.wireOp",EDGE,"E208.MirrorCS"),sQuery(id+"F11.wireOp",EDGE,"E209.MirrorCS"),sQuery(id+"F11.wireOp",EDGE,"E210.MirrorCS"),sQuery(id+"F11.wireOp",EDGE,"E211.MirrorCS"),sQuery(id+"F11.wireOp",EDGE,"E212.MirrorCS"),sQuery(id+"F11.wireOp",EDGE,"E197.top"),sQuery(id+"F11.wireOp",EDGE,"E213.MirrorCS"),sQuery(id+"F11.wireOp",EDGE,"E214.MirrorCS"),sQuery(id+"F11.wireOp",EDGE,"E215.MirrorCS"),sQuery(id+"F11.wireOp",EDGE,"E216.MirrorCS"),sQuery(id+"F11.wireOp",EDGE,"E217.MirrorCS"),sQuery(id+"F11.wireOp",EDGE,"E218.MirrorCS"),sQuery(id+"F11.wireOp",EDGE,"E219.MirrorCS"),sQuery(id+"F11.wireOp",EDGE,"E220.MirrorCS"),sQuery(id+"F11.wireOp",EDGE,"E221.MirrorCS"),sQuery(id+"F11.wireOp",EDGE,"E222.trimOffspring"),sQuery(id+"F11.wireOp",EDGE,"E223.trimOffspring"),sQuery(id+"F11.wireOp",EDGE,"E224.trimOffspring"),sQuery(id+"F11.wireOp",EDGE,"E225.trimOffspring"),sQuery(id+"F11.wireOp",EDGE,"E227.trimOffspring"),sQuery(id+"F11.wireOp",EDGE,"E228.trimOffspring"),sQuery(id+"F11.wireOp",EDGE,"E229.trimOffspring"),sQuery(id+"F11.wireOp",EDGE,"E226.trimOffspring")])]});
            transform(context, id + "F13", {"entities" : qUnion([Q0]), "transformType" : TransformType.TRANSLATION_3D, "dx" : 0 * mm, "dy" : 0 * mm, "dz" : 38 * mm, "makeCopy" : false});
        }
        {
            var Q0;
            Q0=qCreatedBy(makeId("Front.planeOp"),FACE);
            var sketch = newSketch(context, id + "F14", { "sketchPlane" : qUnion([Q0])});
            skLineSegment(sketch, "E230.bottom", {"start": v(0, 3) * mm, "end": v(-5, 3) * mm});
            skLineSegment(sketch, "E230.top", {"start": v(0, 38) * mm, "end": v(-38, 38) * mm});
            skLineSegment(sketch, "E230.left", {"start": v(0, 3) * mm, "end": v(0, 38) * mm});
            skLineSegment(sketch, "E230.right", {"start": v(-38, 3) * mm, "end": v(-38, 38) * mm});
            skLineSegment(sketch, "E231", {"start": v(-33, 3) * mm, "end": v(-33, 6) * mm});
            skLineSegment(sketch, "E232", {"start": v(-33, 6) * mm, "end": v(-25, 6) * mm});
            skLineSegment(sketch, "E233", {"start": v(-25, 6) * mm, "end": v(-25, 3) * mm});
            skLineSegment(sketch, "E234", {"start": v(-13, 3) * mm, "end": v(-13, 6) * mm});
            skLineSegment(sketch, "E235", {"start": v(-13, 6) * mm, "end": v(-5, 6) * mm});
            skLineSegment(sketch, "E236", {"start": v(-5, 6) * mm, "end": v(-5, 3) * mm});
            skLineSegment(sketch, "E237.trimOffspring", {"start": v(-33, 3) * mm, "end": v(-38, 3) * mm});
            skLineSegment(sketch, "E238.trimOffspring", {"start": v(-13, 3) * mm, "end": v(-25, 3) * mm});
            skSolve(sketch);
        }
        {
            var Q0;
            Q0=makeQuery(id+"F14.imprint","IMPRINT",FACE,{"disambiguationData":[TD([[makeQuery(id+"F14.imprint","IMPRINT",EDGE,{"derivedFrom":sQuery(id+"F14.wireOp",EDGE,"E230.bottom")}),-1.0]])]});
            extrude(context, id + "F15", {"entities" : qUnion([Q0]), "depth" : (getVariable(context, 'WoodWidth')) * mm});
        }
    });
